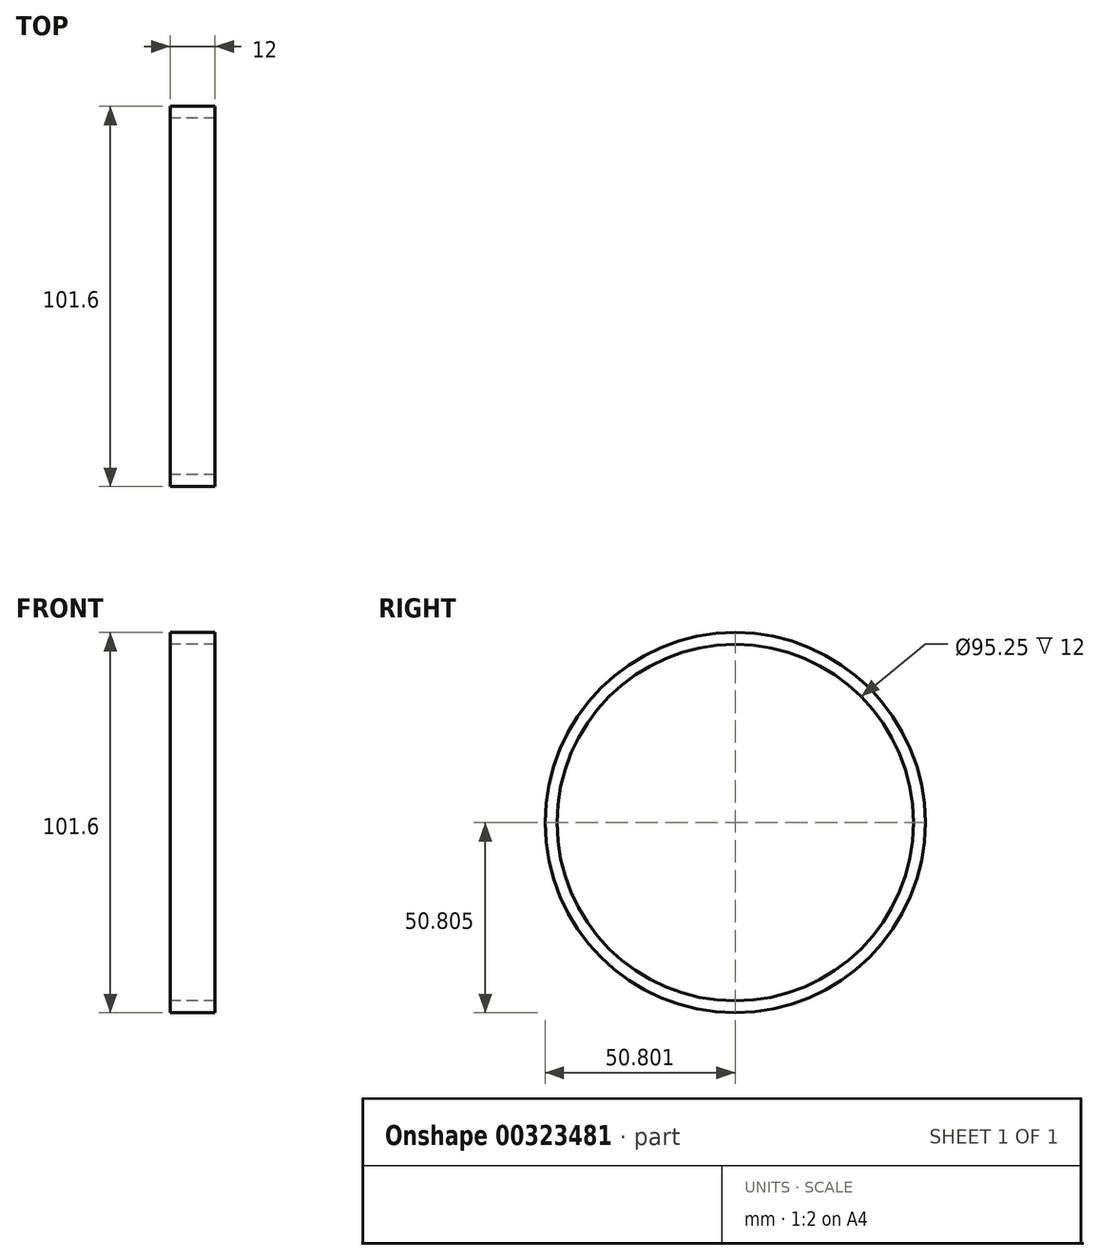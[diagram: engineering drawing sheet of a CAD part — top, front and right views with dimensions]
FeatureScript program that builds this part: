
annotation { "Feature Type Name" : "Feature", "Feature Type Description" : "" }
export const myFeature = defineFeature(function(context is Context, id is Id, definition is map)
    precondition{}
    {
        {
            assignVariable(context, id + "F0", {"name" : "length", "anyValue" : 12});
        }
        {
            var Q0;
            Q0=qCreatedBy(makeId("Right.planeOp"),FACE);
            var sketch = newSketch(context, id + "F1", { "sketchPlane" : qUnion([Q0])});
            skCircle(sketch, "E0", {"center": v(13.93, 20.1) * mm, "radius": 50.8 * mm});
            skCircle(sketch, "E1", {"center": v(13.93, 20.1) * mm, "radius": 47.63 * mm});
            skSolve(sketch);
        }
        {
            var Q0;
            Q0=makeQuery(id+"F1.imprint","IMPRINT",FACE,{"disambiguationData":[TD([[makeQuery(id+"F1.imprint","IMPRINT",EDGE,{"derivedFrom":sQuery(id+"F1.wireOp",EDGE,"E0")}),1.0]])]});
            extrude(context, id + "F2", {"entities" : qUnion([Q0]), "depth" : (getVariable(context, 'length')) * mm});
        }
    });
